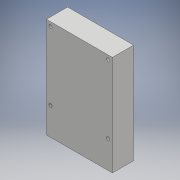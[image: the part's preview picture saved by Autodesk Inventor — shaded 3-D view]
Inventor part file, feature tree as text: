
AUTODESK INVENTOR PART (.ipt)
format: ipt  version: 2017 (Build 210142000, 142)  size: 109,056 bytes
history: native  units: mm
features: extrude x2, sketch x2
ambient origin geometry x8: Origin, YZ Plane, XZ Plane, XY Plane, X Axis, Y Axis, Z Axis, Center Point
bodies: Solid1 (feature_tree)
feature tree (4):
  extrude  "Extrusion1"  Depth=56.0mm
  extrude  "Extrusion2"  Depth=18.0mm
  sketch  "Sketch1"  dims[d0=85.0mm d1=56.0mm]
  sketch  "Sketch2"  dims[d2=18.0mm d3=0.0mm d4=3.5mm d5=3.5mm d6=58.0mm d7=2.75mm d8=3.5mm d9=18.0mm d10=0.0mm]
